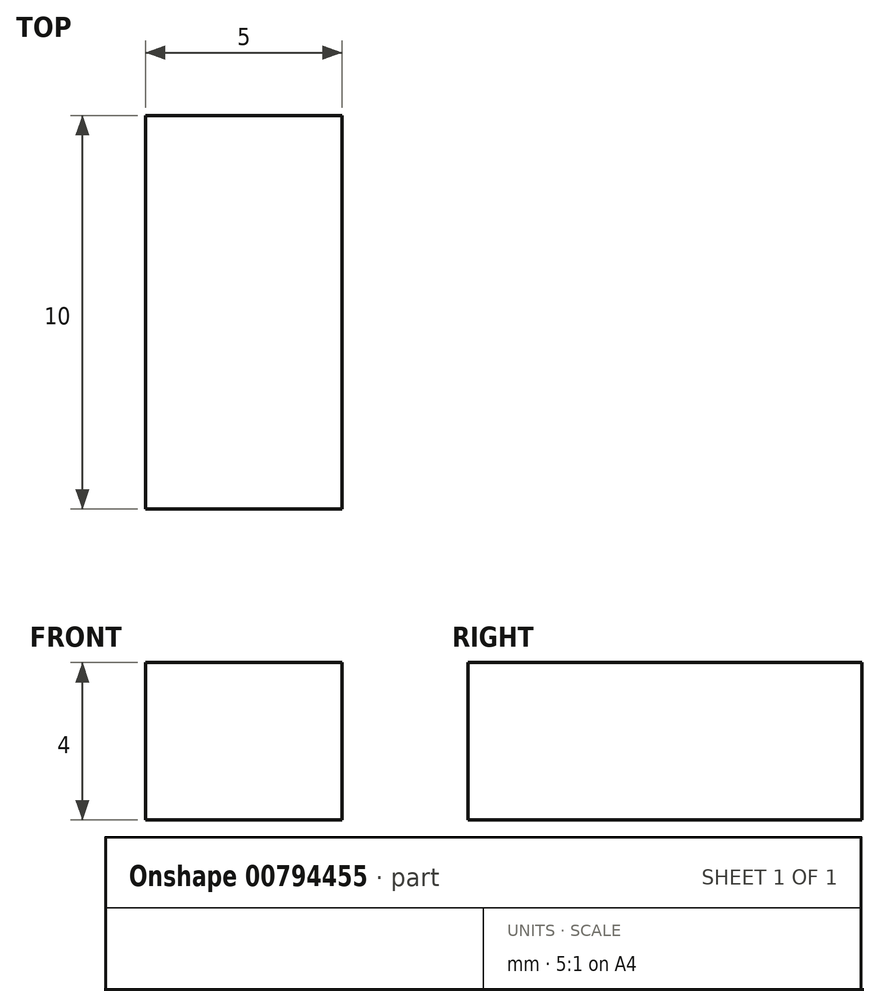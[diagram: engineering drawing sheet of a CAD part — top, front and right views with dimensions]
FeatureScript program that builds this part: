
annotation { "Feature Type Name" : "Feature", "Feature Type Description" : "" }
export const myFeature = defineFeature(function(context is Context, id is Id, definition is map)
    precondition{}
    {
        {
            var Q0;
            Q0=qCreatedBy(makeId("Top.planeOp"),FACE);
            var sketch = newSketch(context, id + "F0", { "sketchPlane" : qUnion([Q0])});
            skLineSegment(sketch, "E0.bottom", {"start": v(0, 0) * mm, "end": v(5, 0) * mm});
            skLineSegment(sketch, "E0.top", {"start": v(0, -10) * mm, "end": v(5, -10) * mm});
            skLineSegment(sketch, "E0.left", {"start": v(0, 0) * mm, "end": v(0, -10) * mm});
            skLineSegment(sketch, "E0.right", {"start": v(5, 0) * mm, "end": v(5, -10) * mm});
            skSolve(sketch);
        }
        {
            var Q0;
            Q0 = qSketchRegion(id + "F0", true);
            extrude(context, id + "F1", {"entities" : qUnion([Q0]), "depth" : 4 * mm, "offsetDistance" : 25 * mm});
        }
    });
